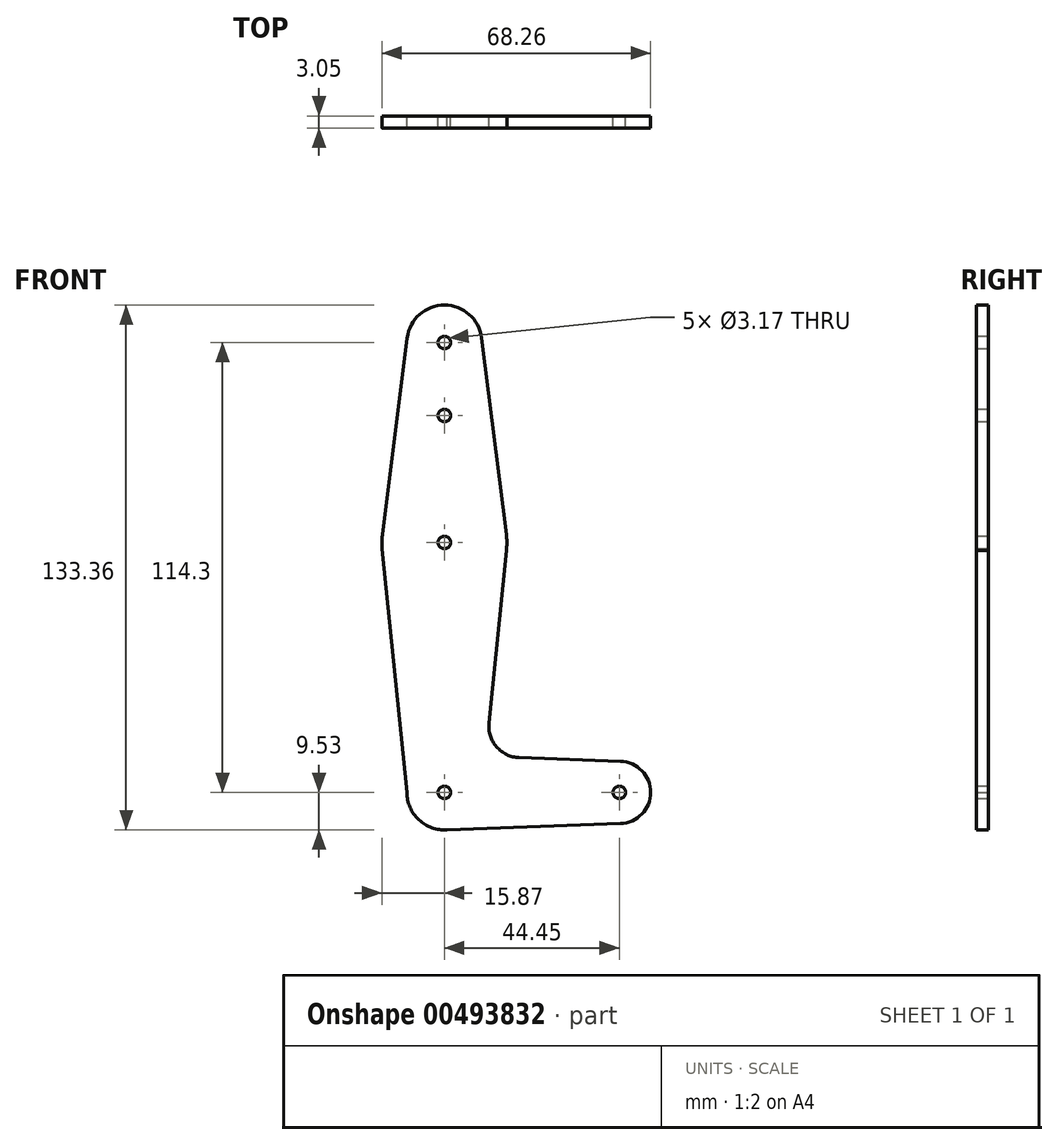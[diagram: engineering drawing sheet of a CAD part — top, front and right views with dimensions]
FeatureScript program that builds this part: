
annotation { "Feature Type Name" : "Feature", "Feature Type Description" : "" }
export const myFeature = defineFeature(function(context is Context, id is Id, definition is map)
    precondition{}
    {
        {
            var Q0;
            Q0=qCreatedBy(makeId("Front.planeOp"),FACE);
            var sketch = newSketch(context, id + "F0", { "sketchPlane" : qUnion([Q0])});
            skLineSegment(sketch, "E0", {"start": v(0, 0) * mm, "end": v(0, 114.3) * mm});
            skLineSegment(sketch, "E1", {"start": v(0, 0) * mm, "end": v(44.45, 0) * mm});
            skCircle(sketch, "E2", {"center": v(0, 114.3) * mm, "radius": 9.53 * mm});
            skCircle(sketch, "E3", {"center": v(0, 0) * mm, "radius": 9.53 * mm});
            skCircle(sketch, "E4", {"center": v(0, 63.5) * mm, "radius": 15.88 * mm});
            skCircle(sketch, "E5", {"center": v(44.45, 0) * mm, "radius": 7.94 * mm});
            skLineSegment(sketch, "E6", {"start": v(9.45, 115.5) * mm, "end": v(15.75, 65.48) * mm});
            skLineSegment(sketch, "E7", {"start": v(-9.45, 115.5) * mm, "end": v(-15.75, 65.48) * mm});
            skLineSegment(sketch, "E8", {"start": v(15.75, 61.52) * mm, "end": v(11.34, 17.59) * mm});
            skLineSegment(sketch, "E9", {"start": v(18.97, 8.85) * mm, "end": v(44.73, 7.93) * mm});
            skLineSegment(sketch, "E10", {"start": v(0, -9.53) * mm, "end": v(44.73, -7.93) * mm});
            skCircle(sketch, "E11", {"center": v(0, 114.3) * mm, "radius": 1.59 * mm});
            skCircle(sketch, "E12", {"center": v(0, 63.5) * mm, "radius": 1.59 * mm});
            skCircle(sketch, "E13", {"center": v(0, 0) * mm, "radius": 1.59 * mm});
            skCircle(sketch, "E14", {"center": v(44.45, 0) * mm, "radius": 1.59 * mm});
            skCircle(sketch, "E15", {"center": v(0, 95.76) * mm, "radius": 1.59 * mm});
            skArc(sketch, "E16.filletArc", {"start": v(11.34, 17.59) * mm, "mid": v(13.26, 11.57) * mm, "end": v(18.97, 8.85) * mm});
            skLineSegment(sketch, "E17", {"start": v(-15.8, 61.9) * mm, "end": v(-9.52, 0) * mm});
            skSolve(sketch);
        }
        {
            var Q0;
            Q0 = qSketchRegion(id + "F0", true);
            var Q1;
            {var subQ0=sQuery(id+"F0.wireOp",EDGE,"E13");var subQ1=sQuery(id+"F0.wireOp",EDGE,"E0");var subQ2=makeQuery(id+"F0.imprint","INTERSECT",VERTEX,{"derivedFrom":[subQ1,subQ0]});Q1=makeQuery(id+"F0.imprint","IMPRINT",FACE,{"disambiguationData":[TD([[makeQuery(id+"F0.imprint","IMPRINT",EDGE,{"disambiguationData":[TD([[subQ2,-1.0]])],"derivedFrom":subQ1}),-1.0]])]});}
            extrude(context, id + "F1", {"entities" : qUnion([Q0, Q1]), "depth" : 3.05 * mm});
        }
    });
